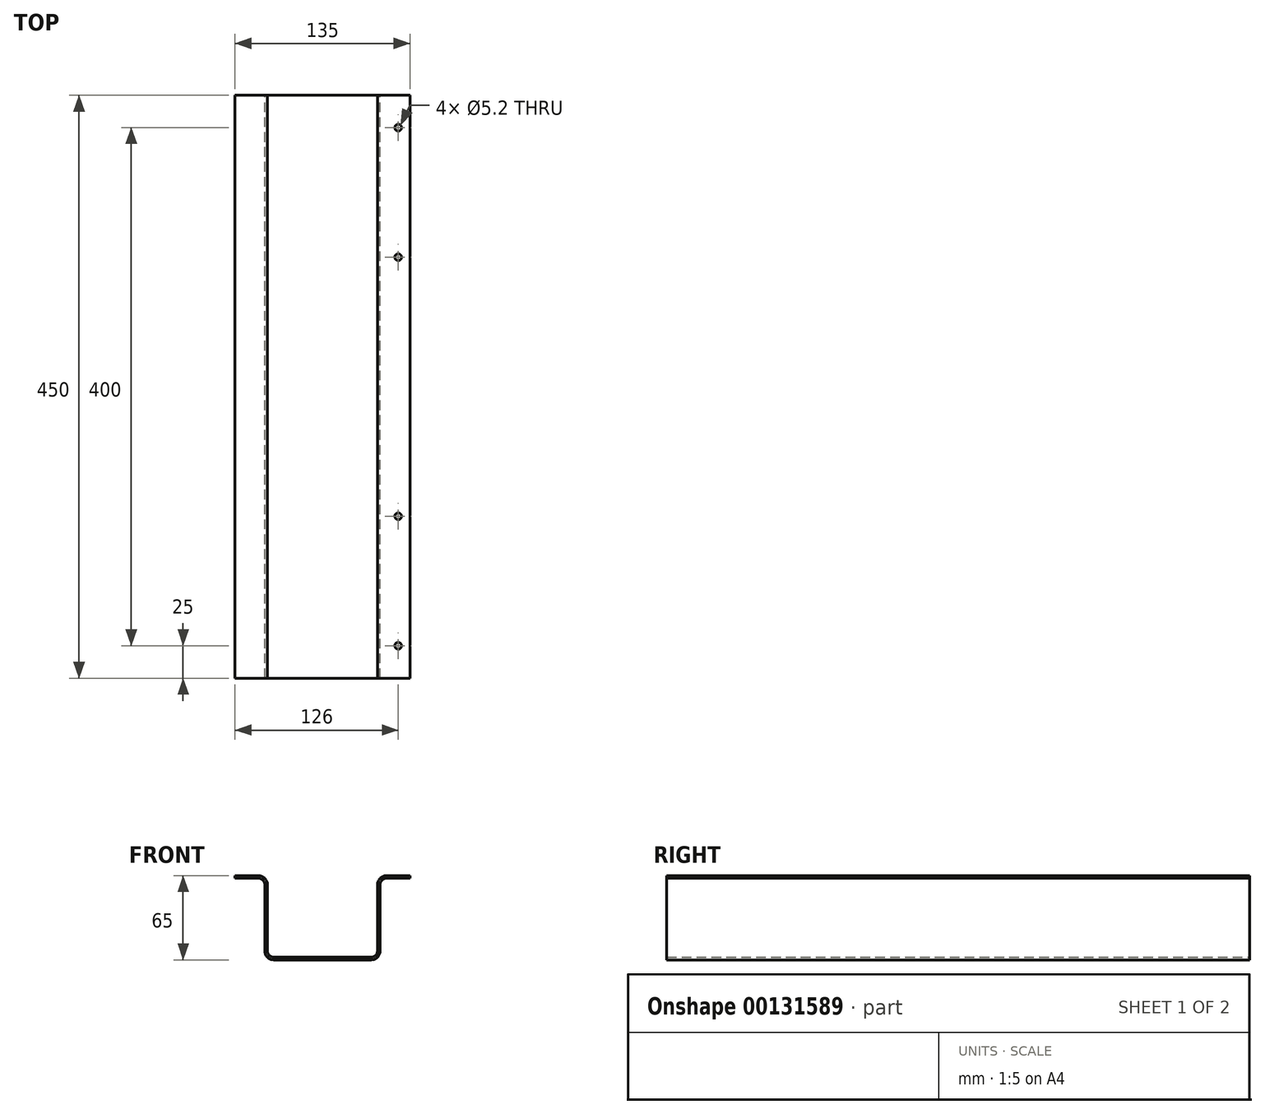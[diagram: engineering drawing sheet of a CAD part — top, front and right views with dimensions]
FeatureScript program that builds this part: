
annotation { "Feature Type Name" : "Feature", "Feature Type Description" : "" }
export const myFeature = defineFeature(function(context is Context, id is Id, definition is map)
    precondition{}
    {
        {
            var Q0;
            Q0=qCreatedBy(makeId("Front.planeOp"),FACE);
            var sketch = newSketch(context, id + "F0", { "sketchPlane" : qUnion([Q0])});
            skLineSegment(sketch, "E0", {"start": v(-67.5, 0) * mm, "end": v(-44.5, 0) * mm});
            skLineSegment(sketch, "E1", {"start": v(-44.5, 0) * mm, "end": v(-44.5, -63) * mm});
            skLineSegment(sketch, "E2", {"start": v(-44.5, -63) * mm, "end": v(0, -63) * mm});
            skLineSegment(sketch, "E3", {"start": v(-67.5, 0) * mm, "end": v(-67.5, 2) * mm});
            skLineSegment(sketch, "E4", {"start": v(-67.5, 2) * mm, "end": v(-42.5, 2) * mm});
            skLineSegment(sketch, "E5", {"start": v(-42.5, 2) * mm, "end": v(-42.5, -61) * mm});
            skLineSegment(sketch, "E6", {"start": v(-42.5, -61) * mm, "end": v(0, -61) * mm});
            skLineSegment(sketch, "E7.MirrorCS", {"start": v(67.5, 0) * mm, "end": v(67.5, 2) * mm});
            skLineSegment(sketch, "E8.MirrorCS", {"start": v(67.5, 2) * mm, "end": v(42.5, 2) * mm});
            skLineSegment(sketch, "E9.MirrorCS", {"start": v(42.5, 2) * mm, "end": v(42.5, -61) * mm});
            skLineSegment(sketch, "E10.MirrorCS", {"start": v(44.5, 0) * mm, "end": v(44.5, -63) * mm});
            skLineSegment(sketch, "E11.MirrorCS", {"start": v(42.5, -61) * mm, "end": v(0, -61) * mm});
            skLineSegment(sketch, "E12.MirrorCS", {"start": v(44.5, -63) * mm, "end": v(0, -63) * mm});
            skLineSegment(sketch, "E13.MirrorCS", {"start": v(67.5, 0) * mm, "end": v(44.5, 0) * mm});
            skSolve(sketch);
        }
        {
            var Q0;
            Q0=makeQuery(id+"F0.imprint","IMPRINT",FACE,{"disambiguationData":[TD([[makeQuery(id+"F0.imprint","IMPRINT",EDGE,{"derivedFrom":sQuery(id+"F0.wireOp",EDGE,"E0")}),1.0]])]});
            extrude(context, id + "F1", {"entities" : qUnion([Q0]), "depth" : 450 * mm});
        }
        {
            var Q0;
            Q0=makeQuery(id+"F1.opExtrude","SWEPT_EDGE",EDGE,{"disambiguationData":[OSD([sQuery(id+"F0.wireOp",EDGE,"E5"),sQuery(id+"F0.wireOp",EDGE,"E6")])]});
            var Q1;
            Q1=makeQuery(id+"F1.opExtrude","SWEPT_EDGE",EDGE,{"disambiguationData":[OSD([sQuery(id+"F0.wireOp",EDGE,"E10.MirrorCS"),sQuery(id+"F0.wireOp",EDGE,"E13.MirrorCS")])]});
            var Q2;
            Q2=makeQuery(id+"F1.opExtrude","SWEPT_EDGE",EDGE,{"disambiguationData":[OSD([sQuery(id+"F0.wireOp",EDGE,"E0"),sQuery(id+"F0.wireOp",EDGE,"E1")])]});
            var Q3;
            Q3=makeQuery(id+"F1.opExtrude","SWEPT_EDGE",EDGE,{"disambiguationData":[OSD([sQuery(id+"F0.wireOp",EDGE,"E9.MirrorCS"),sQuery(id+"F0.wireOp",EDGE,"E11.MirrorCS")])]});
            fillet(context, id + "F2", {"entities" : qUnion([Q0, Q1, Q2, Q3]), "radius" : 5 * mm, "tangentPropagation" : true, "allowEdgeOverflow" : false});
        }
        {
            var Q0;
            Q0=makeQuery(id+"F1.opExtrude","SWEPT_EDGE",EDGE,{"disambiguationData":[OSD([sQuery(id+"F0.wireOp",EDGE,"E4"),sQuery(id+"F0.wireOp",EDGE,"E5")])]});
            var Q1;
            Q1=makeQuery(id+"F1.opExtrude","SWEPT_EDGE",EDGE,{"disambiguationData":[OSD([sQuery(id+"F0.wireOp",EDGE,"E10.MirrorCS"),sQuery(id+"F0.wireOp",EDGE,"E12.MirrorCS")])]});
            var Q2;
            Q2=makeQuery(id+"F1.opExtrude","SWEPT_EDGE",EDGE,{"disambiguationData":[OSD([sQuery(id+"F0.wireOp",EDGE,"E8.MirrorCS"),sQuery(id+"F0.wireOp",EDGE,"E9.MirrorCS")])]});
            var Q3;
            Q3=makeQuery(id+"F1.opExtrude","SWEPT_EDGE",EDGE,{"disambiguationData":[OSD([sQuery(id+"F0.wireOp",EDGE,"E1"),sQuery(id+"F0.wireOp",EDGE,"E2")])]});
            fillet(context, id + "F3", {"entities" : qUnion([Q0, Q1, Q2, Q3]), "radius" : 7 * mm, "tangentPropagation" : true, "allowEdgeOverflow" : false});
        }
        {
            var Q0;
            Q0=makeQuery(id+"F1.opExtrude","SWEPT_FACE",FACE,{"disambiguationData":[OSD([sQuery(id+"F0.wireOp",EDGE,"E8.MirrorCS")])]});
            var sketch = newSketch(context, id + "F4", { "sketchPlane" : qUnion([Q0])});
            skCircle(sketch, "E14", {"center": v(58.5, -425) * mm, "radius": 2.6 * mm});
            skPoint(sketch, "E14.centerSnap0", {"position": v(58.5, -450) * mm});
            skCircle(sketch, "E15", {"center": v(58.5, -325) * mm, "radius": 2.6 * mm});
            skCircle(sketch, "E16", {"center": v(58.5, -125) * mm, "radius": 2.6 * mm});
            skCircle(sketch, "E17", {"center": v(58.5, -25) * mm, "radius": 2.6 * mm});
            skLineSegment(sketch, "E18", {"start": v(67.5, -450) * mm, "end": v(0, -450) * mm, "construction": true});
            skLineSegment(sketch, "E19", {"start": v(0, -450) * mm, "end": v(0, 0) * mm, "construction": true});
            skCircle(sketch, "E20.MirrorC", {"center": v(-58.5, -25) * mm, "radius": 2.6 * mm});
            skCircle(sketch, "E21.MirrorC", {"center": v(-58.5, -125) * mm, "radius": 2.6 * mm});
            skCircle(sketch, "E22.MirrorC", {"center": v(-58.5, -325) * mm, "radius": 2.6 * mm});
            skCircle(sketch, "E23.MirrorC", {"center": v(-58.5, -425) * mm, "radius": 2.6 * mm});
            skSolve(sketch);
        }
        {
            var Q0;
            Q0=makeQuery(id+"F4.imprint","IMPRINT",FACE,{"disambiguationData":[TD([[makeQuery(id+"F4.imprint","IMPRINT",EDGE,{"derivedFrom":sQuery(id+"F4.wireOp",EDGE,"E14")}),1.0]])]});
            var Q1;
            Q1=makeQuery(id+"F4.imprint","IMPRINT",FACE,{"disambiguationData":[TD([[makeQuery(id+"F4.imprint","IMPRINT",EDGE,{"derivedFrom":sQuery(id+"F4.wireOp",EDGE,"E15")}),1.0]])]});
            var Q2;
            Q2=makeQuery(id+"F4.imprint","IMPRINT",FACE,{"disambiguationData":[TD([[makeQuery(id+"F4.imprint","IMPRINT",EDGE,{"derivedFrom":sQuery(id+"F4.wireOp",EDGE,"E16")}),1.0]])]});
            var Q3;
            Q3=makeQuery(id+"F4.imprint","IMPRINT",FACE,{"disambiguationData":[TD([[makeQuery(id+"F4.imprint","IMPRINT",EDGE,{"derivedFrom":sQuery(id+"F4.wireOp",EDGE,"E17")}),1.0]])]});
            var Q4;
            Q4=makeQuery(id+"F4.imprint","IMPRINT",FACE,{"disambiguationData":[TD([[makeQuery(id+"F4.imprint","IMPRINT",EDGE,{"derivedFrom":sQuery(id+"F4.wireOp",EDGE,"E20.MirrorC")}),-1.0]])]});
            var Q5;
            Q5=makeQuery(id+"F4.imprint","IMPRINT",FACE,{"disambiguationData":[TD([[makeQuery(id+"F4.imprint","IMPRINT",EDGE,{"derivedFrom":sQuery(id+"F4.wireOp",EDGE,"E21.MirrorC")}),-1.0]])]});
            var Q6;
            Q6=makeQuery(id+"F4.imprint","IMPRINT",FACE,{"disambiguationData":[TD([[makeQuery(id+"F4.imprint","IMPRINT",EDGE,{"derivedFrom":sQuery(id+"F4.wireOp",EDGE,"E22.MirrorC")}),-1.0]])]});
            var Q7;
            Q7=makeQuery(id+"F4.imprint","IMPRINT",FACE,{"disambiguationData":[TD([[makeQuery(id+"F4.imprint","IMPRINT",EDGE,{"derivedFrom":sQuery(id+"F4.wireOp",EDGE,"E23.MirrorC")}),-1.0]])]});
            extrude(context, id + "F5", {"entities" : qUnion([Q0, Q1, Q2, Q3, Q4, Q5, Q6, Q7]), "operationType" : NewBodyOperationType.REMOVE, "oppositeDirection" : true, "depth" : 25 * mm});
        }
    });
